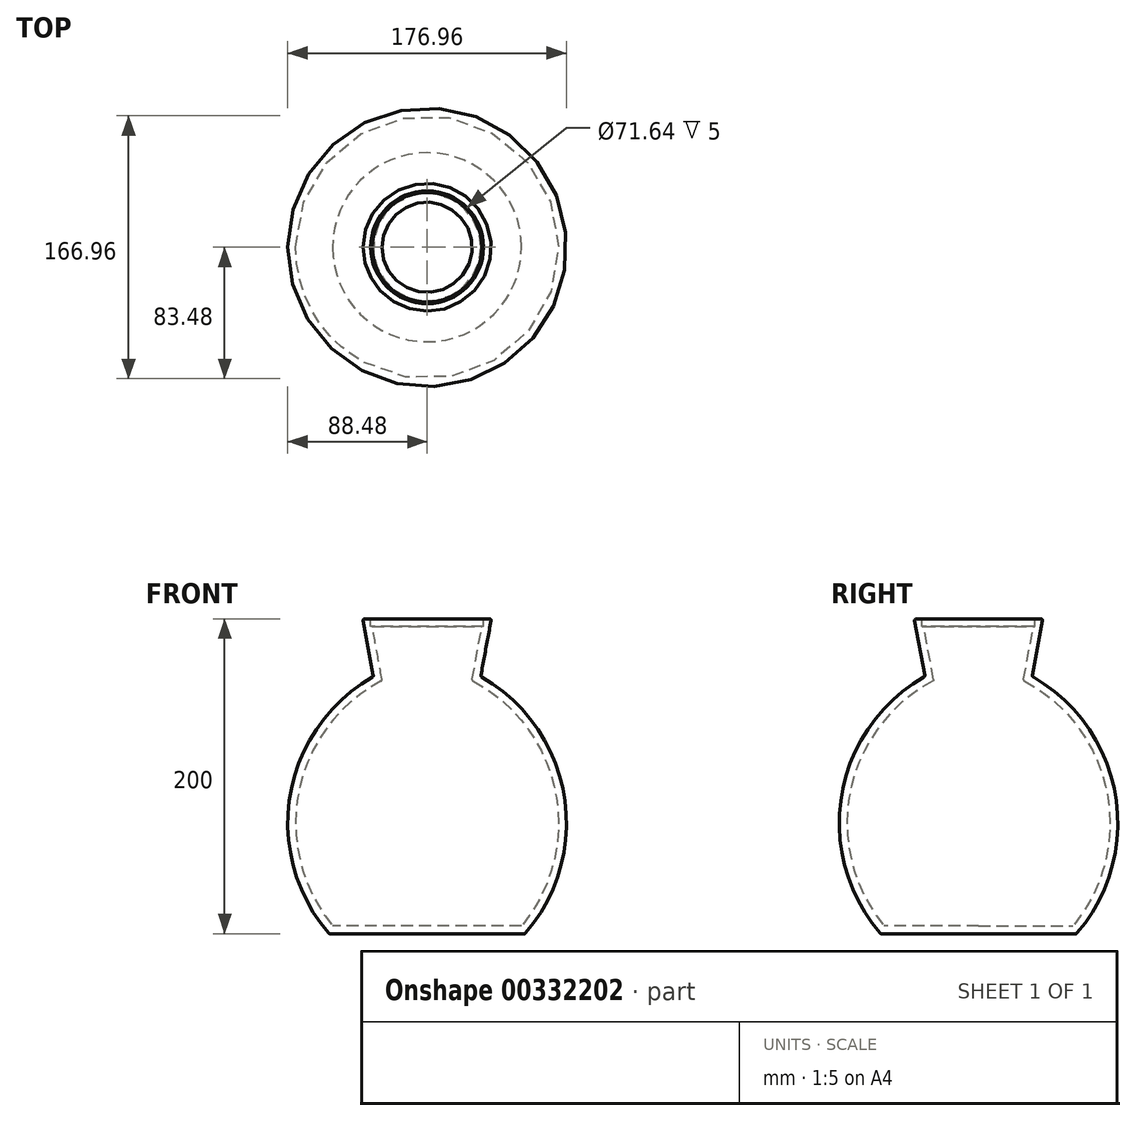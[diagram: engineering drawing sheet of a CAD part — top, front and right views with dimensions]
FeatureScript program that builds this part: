
annotation { "Feature Type Name" : "Feature", "Feature Type Description" : "" }
export const myFeature = defineFeature(function(context is Context, id is Id, definition is map)
    precondition{}
    {
        {
            var Q0;
            Q0=qCreatedBy(makeId("Front.planeOp"),FACE);
            var sketch = newSketch(context, id + "F0", { "sketchPlane" : qUnion([Q0])});
            skLineSegment(sketch, "E0", {"start": v(0, 0) * mm, "end": v(62.32, 0) * mm});
            skArc(sketch, "E1", {"start": v(62.32, 0) * mm, "mid": v(86.92, 88.4) * mm, "end": v(34.05, 163.4) * mm});
            skLineSegment(sketch, "E2", {"start": v(34.05, 163.4) * mm, "end": v(40.82, 200) * mm});
            skLineSegment(sketch, "E3", {"start": v(40.82, 200) * mm, "end": v(0, 200) * mm});
            skLineSegment(sketch, "E4", {"start": v(0, 200) * mm, "end": v(0, 0) * mm});
            skSolve(sketch);
        }
        {
            var Q0;
            Q0 = qSketchRegion(id + "F0", true);
            var Q1;
            Q1=sQuery(id+"F0.wireOp",EDGE,"E4");
            revolve(context, id + "F1", {"surfaceOperationType" : NewSurfaceOperationType.NEW, "entities" : qUnion([Q0]), "axis" : qUnion([Q1]), "revolveType" : RevolveType.FULL});
        }
        {
            var Q0;
            Q0=makeQuery(id+"F1.opRevolve","SWEPT_FACE",FACE,{"disambiguationData":[OSD([sQuery(id+"F0.wireOp",EDGE,"E3")])]});
            var Q1;
            Q1=makeQuery(id+"F1.opRevolve","SWEPT_BODY",BODY,{"disambiguationData":[OSD([sQuery(id+"F0.wireOp",EDGE,"E0"),sQuery(id+"F0.wireOp",EDGE,"E1"),sQuery(id+"F0.wireOp",EDGE,"E2"),sQuery(id+"F0.wireOp",EDGE,"E3"),sQuery(id+"F0.wireOp",EDGE,"E4")])]});
            shell(context, id + "F2", {"isHollow" : true, "entities" : qUnion([Q0]), "parts" : qUnion([Q1]), "thickness" : 5 * mm});
        }
        {
            var Q0;
            Q0=makeQuery(id+"F1.opRevolve","SWEPT_FACE",FACE,{"disambiguationData":[OSD([sQuery(id+"F0.wireOp",EDGE,"E3")])]});
            var sketch = newSketch(context, id + "F3", { "sketchPlane" : qUnion([Q0])});
            skCircle(sketch, "E5", {"center": v(0, 0) * mm, "radius": 35.82 * mm});
            skSolve(sketch);
        }
        {
            var Q0;
            Q0 = qSketchRegion(id + "F3", true);
            extrude(context, id + "F4", {"entities" : qUnion([Q0]), "operationType" : NewBodyOperationType.REMOVE, "oppositeDirection" : true, "depth" : 5 * mm, "offsetDistance" : 25 * mm});
        }
        {
            var Q0;
            Q0=makeQuery(id+"F2.opShell","OFFSET_EDGE",EDGE,{"disambiguationData":[OSD([sQuery(id+"F0.wireOp",EDGE,"E2"),sQuery(id+"F0.wireOp",EDGE,"E3")])]});
            var Q1;
            Q1=makeQuery(id+"F1.opRevolve","SWEPT_EDGE",EDGE,{"disambiguationData":[OSD([sQuery(id+"F0.wireOp",EDGE,"E1"),sQuery(id+"F0.wireOp",EDGE,"E2")])]});
            var Q2;
            Q2=makeQuery(id+"F1.opRevolve","SWEPT_EDGE",EDGE,{"disambiguationData":[OSD([sQuery(id+"F0.wireOp",EDGE,"E2"),sQuery(id+"F0.wireOp",EDGE,"E3")])]});
            var Q3;
            Q3=makeQuery(id+"F4.boolean.opBoolean","COPY",EDGE,{"derivedFrom":makeQuery(id+"F4.opExtrude","CAP_EDGE",EDGE,{"disambiguationData":[OSD([sQuery(id+"F3.wireOp",EDGE,"E5")])],"isStart":true})});
            var Q4;
            Q4=makeQuery(id+"F1.opRevolve","SWEPT_EDGE",EDGE,{"disambiguationData":[OSD([sQuery(id+"F0.wireOp",EDGE,"E0"),sQuery(id+"F0.wireOp",EDGE,"E1")])]});
            var Q5;
            Q5=makeQuery(id+"F2.opShell","OFFSET_EDGE",EDGE,{"disambiguationData":[OSD([sQuery(id+"F0.wireOp",EDGE,"E1"),sQuery(id+"F0.wireOp",EDGE,"E2")])]});
            fillet(context, id + "F5", {"entities" : qUnion([Q0, Q1, Q2, Q3, Q4, Q5]), "tangentPropagation" : true, "radius" : 1 * mm, "defaultsChanged" : false, "vertexSettings" : [], "allowEdgeOverflow" : false});
        }
    });
